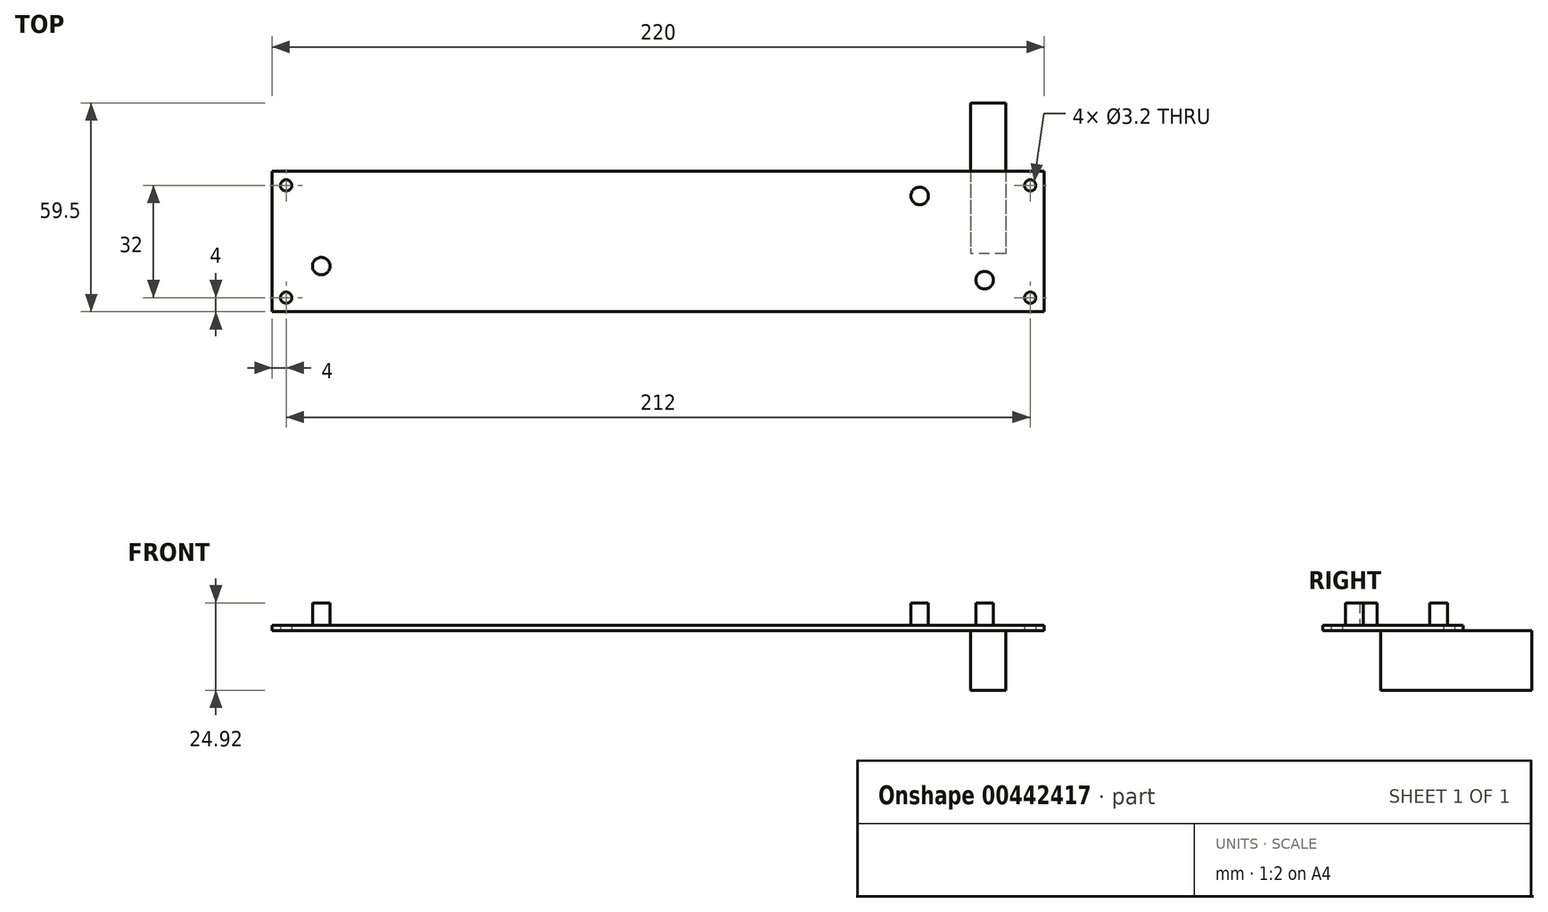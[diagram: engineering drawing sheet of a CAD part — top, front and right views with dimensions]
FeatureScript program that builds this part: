
annotation { "Feature Type Name" : "Feature", "Feature Type Description" : "" }
export const myFeature = defineFeature(function(context is Context, id is Id, definition is map)
    precondition{}
    {
        {
            var Q0;
            Q0=qCreatedBy(makeId("Top.planeOp"),FACE);
            var sketch = newSketch(context, id + "F0", { "sketchPlane" : qUnion([Q0])});
            skLineSegment(sketch, "E0.bottom", {"start": v(-110, 20) * mm, "end": v(110, 20) * mm});
            skLineSegment(sketch, "E0.top", {"start": v(-110, -20) * mm, "end": v(110, -20) * mm});
            skLineSegment(sketch, "E0.left", {"start": v(-110, 20) * mm, "end": v(-110, -20) * mm});
            skLineSegment(sketch, "E0.right", {"start": v(110, 20) * mm, "end": v(110, -20) * mm});
            skPoint(sketch, "E0.middle", {"position": v(0, 0) * mm});
            skCircle(sketch, "E1", {"center": v(-106, 16) * mm, "radius": 1.6 * mm});
            skCircle(sketch, "E2", {"center": v(-106, -16) * mm, "radius": 1.6 * mm});
            skLineSegment(sketch, "E3", {"start": v(0, 0) * mm, "end": v(0, 20) * mm, "construction": true});
            skCircle(sketch, "E4.MirrorC", {"center": v(106, 16) * mm, "radius": 1.6 * mm});
            skCircle(sketch, "E5.MirrorC", {"center": v(106, -16) * mm, "radius": 1.6 * mm});
            skSolve(sketch);
        }
        {
            var Q0;
            Q0 = qSketchRegion(id + "F0", true);
            extrude(context, id + "F1", {"entities" : qUnion([Q0]), "depth" : 1.57 * mm});
        }
        {
            var Q0;
            Q0=makeQuery(id+"F1.opExtrude","CAP_FACE",FACE,{"disambiguationData":[OSD([sQuery(id+"F0.wireOp",EDGE,"E0.bottom"),sQuery(id+"F0.wireOp",EDGE,"E0.top"),sQuery(id+"F0.wireOp",EDGE,"E0.left"),sQuery(id+"F0.wireOp",EDGE,"E0.right"),sQuery(id+"F0.wireOp",EDGE,"E1"),sQuery(id+"F0.wireOp",EDGE,"E2"),sQuery(id+"F0.wireOp",EDGE,"E4.MirrorC"),sQuery(id+"F0.wireOp",EDGE,"E5.MirrorC")])],"isStart":true});
            var sketch = newSketch(context, id + "F2", { "sketchPlane" : qUnion([Q0])});
            skLineSegment(sketch, "E6", {"start": v(0, 0) * mm, "end": v(110, 0) * mm, "construction": true});
            skLineSegment(sketch, "E7.bottom", {"start": v(99, -19.5) * mm, "end": v(89, -19.5) * mm});
            skLineSegment(sketch, "E7.top", {"start": v(99, 3.5) * mm, "end": v(89, 3.5) * mm});
            skLineSegment(sketch, "E7.left", {"start": v(99, -19.5) * mm, "end": v(99, 3.5) * mm});
            skLineSegment(sketch, "E7.right", {"start": v(89, -19.5) * mm, "end": v(89, 3.5) * mm});
            skPoint(sketch, "E7.middle", {"position": v(94, -8) * mm});
            skSolve(sketch);
        }
        {
            var Q0;
            Q0 = qSketchRegion(id + "F2", true);
            extrude(context, id + "F3", {"entities" : qUnion([Q0]), "operationType" : NewBodyOperationType.ADD, "depth" : 17 * mm});
        }
        {
            var Q0;
            Q0=makeQuery(id+"F3.opExtrude","SWEPT_FACE",FACE,{"disambiguationData":[OSD([sQuery(id+"F2.wireOp",EDGE,"E7.bottom")])]});
            extrude(context, id + "F4", {"entities" : qUnion([Q0]), "operationType" : NewBodyOperationType.ADD, "depth" : 20 * mm});
        }
        {
            var Q0;
            Q0=makeQuery(id+"F1.opExtrude","CAP_FACE",FACE,{"disambiguationData":[OSD([sQuery(id+"F0.wireOp",EDGE,"E0.bottom"),sQuery(id+"F0.wireOp",EDGE,"E0.top"),sQuery(id+"F0.wireOp",EDGE,"E0.left"),sQuery(id+"F0.wireOp",EDGE,"E0.right"),sQuery(id+"F0.wireOp",EDGE,"E1"),sQuery(id+"F0.wireOp",EDGE,"E2"),sQuery(id+"F0.wireOp",EDGE,"E4.MirrorC"),sQuery(id+"F0.wireOp",EDGE,"E5.MirrorC")])],"isStart":false});
            var sketch = newSketch(context, id + "F5", { "sketchPlane" : qUnion([Q0])});
            skCircle(sketch, "E8", {"center": v(93, -11) * mm, "radius": 2.5 * mm});
            skCircle(sketch, "E9", {"center": v(-96, -7) * mm, "radius": 2.5 * mm});
            skCircle(sketch, "E10", {"center": v(74.5, 13) * mm, "radius": 2.5 * mm});
            skSolve(sketch);
        }
        {
            var Q0;
            Q0 = qSketchRegion(id + "F5", true);
            extrude(context, id + "F6", {"entities" : qUnion([Q0]), "operationType" : NewBodyOperationType.ADD, "depth" : 6.35 * mm});
        }
    });
